# Revit family: Faucet-Bath_Filler-KOHLER-Singulier-K-10873
name_source: partatom
category: Plumbing Fixtures
revit_build: Autodesk Revit 2015 (Build: 20140606_1530(x64)
units: mm (PartAtom-declared; Revit-internal decimal feet)

## types (1)
- CP-Polished Chrome
    ADA Compliant = No
    Assembly Code = D2010
    CW Connection = Yes
    Cold Water Inlet = Cold Water Inlet
    Date Modified = 12/11/2018
    Default Elevation = 36"
    Description = Deck-mount bath filler with handshower
    Drain Included = No
    Finish = Kohler-Metal-CP-Polished_Chrome
    Flow Rate = 4 GPM
    HW Connection = Yes
    Height = 9 1/8"
    Hot Water Inlet = Hot Water Inlet
    Length = 5 5/16"
    Manufacturer = KOHLER Co.
    MasterFormat 1995 = 15410
    MasterFormat 2004 = 22.41.39
    Material = Solid Brass Construction
    Model = K-10873-4-CP
    Pressure = 0.00 psi
    Product Documentation Link = http://www.us.kohler.com
    Product Name = Singulier
    Product Page URL = http://www.us.kohler.com
    Spout Reach = 5 5/16"
    URL = https://www.us.kohler.com
    Vent Connection = No
    Waste Connection = No
    Waste Water Outlet = Waste Water Outlet

## geometry (parser evidence)
native form markers: Sweep x11
no freeform markers — native parametric forms only
